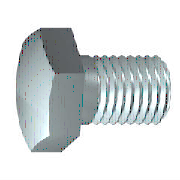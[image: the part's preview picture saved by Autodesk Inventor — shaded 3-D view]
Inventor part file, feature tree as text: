
AUTODESK INVENTOR PART (.ipt)
format: ipt  version: 2023.2 (Build 272271030, 271C)  size: 199,680 bytes
history: native  units: mm (DEFAULTED — no unit token found)
features: sketch x4, other x4, plane x3, chamfer x1, fillet x1
ambient origin geometry x6: Origin, XY Plane, X Axis, Y Axis, Z Axis, Center Point
bodies: Solid1 (feature_tree)
feature tree (13):
  plane  "WorkPlane1"
  sketch  "Sketch1"  dims[d0=30.0mm]
  other  "WorkPoint1"
  chamfer  "Chamfer1"  Distance=7.5mm
  fillet  "Fillet1"  [1 undecoded]
  other  "MSC_A1"
  other  "MSC_PF1"
  other  "MSC_PT1"
  plane  "WorkPlane2"
  plane  "WorkPlane3"
  sketch  "Sketch2"  dims[d1=18.0mm]
  sketch  "Sketch3"  dims[d2=15.0mm]
  sketch  "Sketch4"  dims[d4=17.321016mm d6=7.5mm d7=0.0mm d8=15.0mm d10=0.0mm d12=30.0deg d14=360.0deg d15=0.0mm d17=10.0mm d18=6.0mm d19=80.0mm d20=55.0mm d21=360.0deg d22=0.875mm d23=0.875mm d24=0.6mm d25=0.1mm d26=0.0mm d27=60.0deg d28=9.0mm d29=0.0mm d30=0.0mm d32=0.0mm d33=0.0mm d34=0.0mm d37=0.0mm d38=0.0mm d39=45.0deg d40=0.0mm d41=0.0mm d42=0.0mm]
note: 1 required parameter value undecoded (feature->parameter linkage not recoverable at this tier; creation-order binding heuristic only, values carry confidence <= 0.55)
